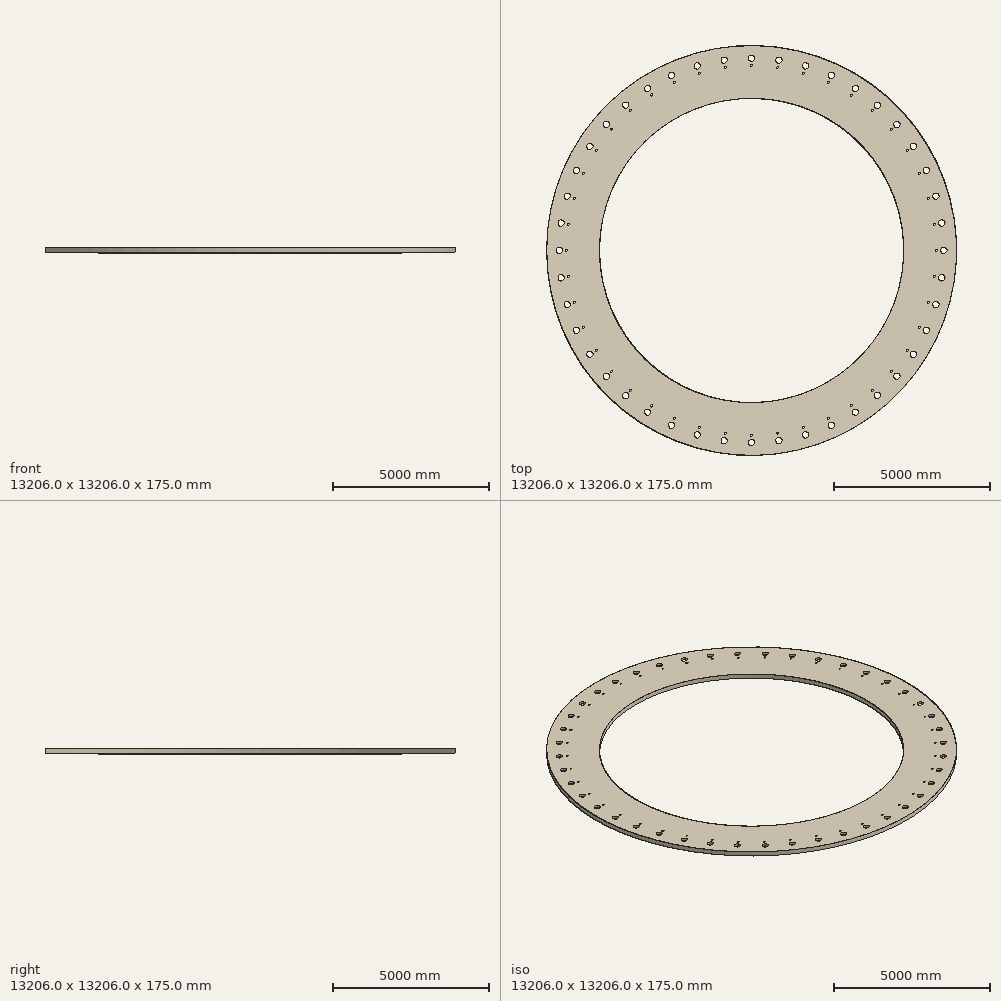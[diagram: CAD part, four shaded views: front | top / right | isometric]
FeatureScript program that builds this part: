
annotation { "Feature Type Name" : "Feature", "Feature Type Description" : "" }
export const myFeature = defineFeature(function(context is Context, id is Id, definition is map)
    precondition{}
    {
        {
            var Q0;
            Q0=qCreatedBy(makeId("Front.planeOp"),FACE);
            var sketch = newSketch(context, id + "F0", { "sketchPlane" : qUnion([Q0])});
            skLineSegment(sketch, "E0", {"start": v(0, 0) * mm, "end": v(0, -150) * mm});
            skLineSegment(sketch, "E1", {"start": v(0, -150) * mm, "end": v(-6, -150) * mm});
            skLineSegment(sketch, "E2", {"start": v(-6, -150) * mm, "end": v(-6, 0) * mm});
            skLineSegment(sketch, "E3", {"start": v(-6, 0) * mm, "end": v(0, 0) * mm});
            skLineSegment(sketch, "E4", {"start": v(-1708, 25) * mm, "end": v(-1708, -125) * mm});
            skLineSegment(sketch, "E5", {"start": v(-1708, -125) * mm, "end": v(-1702, -125) * mm});
            skLineSegment(sketch, "E6", {"start": v(-1702, -125) * mm, "end": v(-1702, 25) * mm});
            skLineSegment(sketch, "E7", {"start": v(-1702, 25) * mm, "end": v(-1708, 25) * mm});
            skLineSegment(sketch, "E8", {"start": v(-1702, 25) * mm, "end": v(-6, 0) * mm});
            skLineSegment(sketch, "E9.0", {"start": v(-1702, -50) * mm, "end": v(-6, -75) * mm});
            skLineSegment(sketch, "E10", {"start": v(0, 0) * mm, "end": v(4895, 0) * mm, "construction": true});
            skPoint(sketch, "E11", {"position": v(4895, 0) * mm});
            skLineSegment(sketch, "E12", {"start": v(4895, 0) * mm, "end": v(4895, 100) * mm, "construction": true});
            skSolve(sketch);
        }
        {
            var Q0;
            Q0 = qSketchRegion(id + "F0", true);
            var Q1;
            Q1=sQuery(id+"F0.wireOp",EDGE,"E12");
            revolve(context, id + "F1", {"surfaceOperationType" : NewSurfaceOperationType.NEW, "entities" : qUnion([Q0]), "axis" : qUnion([Q1]), "revolveType" : RevolveType.FULL});
        }
        {
            var Q0;
            Q0=qCreatedBy(makeId("Top.planeOp"),FACE);
            var sketch = newSketch(context, id + "F2", { "sketchPlane" : qUnion([Q0])});
            skLineSegment(sketch, "E13", {"start": v(0, 0) * mm, "end": v(4895, 0) * mm, "construction": true});
            skLineSegment(sketch, "E14", {"start": v(0, 0) * mm, "end": v(-1055, 0) * mm});
            skLineSegment(sketch, "E15", {"start": v(-1055, 0) * mm, "end": v(-1295, 0) * mm});
            skCircle(sketch, "E16", {"center": v(-1055, 0) * mm, "radius": 35.5 * mm});
            skCircle(sketch, "E17", {"center": v(-1295, 0) * mm, "radius": 102.5 * mm});
            skCircle(sketch, "E18.1.0", {"center": v(-1232, -880.93) * mm, "radius": 102.5 * mm});
            skCircle(sketch, "E18.1.1", {"center": v(-994.44, -846.77) * mm, "radius": 35.5 * mm});
            skCircle(sketch, "E18.2.0", {"center": v(-1044.26, -1743.92) * mm, "radius": 102.5 * mm});
            skCircle(sketch, "E18.2.1", {"center": v(-813.98, -1676.3) * mm, "radius": 35.5 * mm});
            skCircle(sketch, "E18.3.0", {"center": v(-735.62, -2571.42) * mm, "radius": 102.5 * mm});
            skCircle(sketch, "E18.3.1", {"center": v(-517.31, -2471.72) * mm, "radius": 35.5 * mm});
            skCircle(sketch, "E18.4.0", {"center": v(-312.36, -3346.57) * mm, "radius": 102.5 * mm});
            skCircle(sketch, "E18.4.1", {"center": v(-110.46, -3216.81) * mm, "radius": 35.5 * mm});
            skCircle(sketch, "E18.5.0", {"center": v(216.91, -4053.59) * mm, "radius": 102.5 * mm});
            skCircle(sketch, "E18.5.1", {"center": v(398.3, -3896.42) * mm, "radius": 35.5 * mm});
            skCircle(sketch, "E18.6.0", {"center": v(841.41, -4678.09) * mm, "radius": 102.5 * mm});
            skCircle(sketch, "E18.6.1", {"center": v(998.58, -4496.7) * mm, "radius": 35.5 * mm});
            skCircle(sketch, "E18.7.0", {"center": v(1548.43, -5207.36) * mm, "radius": 102.5 * mm});
            skCircle(sketch, "E18.7.1", {"center": v(1678.19, -5005.46) * mm, "radius": 35.5 * mm});
            skCircle(sketch, "E18.8.0", {"center": v(2323.58, -5630.62) * mm, "radius": 102.5 * mm});
            skCircle(sketch, "E18.8.1", {"center": v(2423.28, -5412.31) * mm, "radius": 35.5 * mm});
            skCircle(sketch, "E18.9.0", {"center": v(3151.08, -5939.26) * mm, "radius": 102.5 * mm});
            skCircle(sketch, "E18.9.1", {"center": v(3218.7, -5708.98) * mm, "radius": 35.5 * mm});
            skCircle(sketch, "E18.10.0", {"center": v(4014.07, -6127) * mm, "radius": 102.5 * mm});
            skCircle(sketch, "E18.10.1", {"center": v(4048.23, -5889.44) * mm, "radius": 35.5 * mm});
            skCircle(sketch, "E18.11.0", {"center": v(4895, -6190) * mm, "radius": 102.5 * mm});
            skCircle(sketch, "E18.11.1", {"center": v(4895, -5950) * mm, "radius": 35.5 * mm});
            skCircle(sketch, "E18.12.0", {"center": v(5775.93, -6127) * mm, "radius": 102.5 * mm});
            skCircle(sketch, "E18.12.1", {"center": v(5741.77, -5889.44) * mm, "radius": 35.5 * mm});
            skCircle(sketch, "E18.13.0", {"center": v(6638.92, -5939.26) * mm, "radius": 102.5 * mm});
            skCircle(sketch, "E18.13.1", {"center": v(6571.3, -5708.98) * mm, "radius": 35.5 * mm});
            skCircle(sketch, "E18.14.0", {"center": v(7466.42, -5630.62) * mm, "radius": 102.5 * mm});
            skCircle(sketch, "E18.14.1", {"center": v(7366.72, -5412.31) * mm, "radius": 35.5 * mm});
            skCircle(sketch, "E18.15.0", {"center": v(8241.57, -5207.36) * mm, "radius": 102.5 * mm});
            skCircle(sketch, "E18.15.1", {"center": v(8111.81, -5005.46) * mm, "radius": 35.5 * mm});
            skCircle(sketch, "E18.16.0", {"center": v(8948.59, -4678.09) * mm, "radius": 102.5 * mm});
            skCircle(sketch, "E18.16.1", {"center": v(8791.42, -4496.7) * mm, "radius": 35.5 * mm});
            skCircle(sketch, "E18.17.0", {"center": v(9573.09, -4053.59) * mm, "radius": 102.5 * mm});
            skCircle(sketch, "E18.17.1", {"center": v(9391.7, -3896.42) * mm, "radius": 35.5 * mm});
            skCircle(sketch, "E18.18.0", {"center": v(10102.36, -3346.57) * mm, "radius": 102.5 * mm});
            skCircle(sketch, "E18.18.1", {"center": v(9900.46, -3216.81) * mm, "radius": 35.5 * mm});
            skCircle(sketch, "E18.19.0", {"center": v(10525.62, -2571.42) * mm, "radius": 102.5 * mm});
            skCircle(sketch, "E18.19.1", {"center": v(10307.31, -2471.72) * mm, "radius": 35.5 * mm});
            skCircle(sketch, "E18.20.0", {"center": v(10834.26, -1743.92) * mm, "radius": 102.5 * mm});
            skCircle(sketch, "E18.20.1", {"center": v(10603.98, -1676.3) * mm, "radius": 35.5 * mm});
            skCircle(sketch, "E18.21.0", {"center": v(11022, -880.93) * mm, "radius": 102.5 * mm});
            skCircle(sketch, "E18.21.1", {"center": v(10784.44, -846.77) * mm, "radius": 35.5 * mm});
            skCircle(sketch, "E18.22.0", {"center": v(11085, 0) * mm, "radius": 102.5 * mm});
            skCircle(sketch, "E18.22.1", {"center": v(10845, 0) * mm, "radius": 35.5 * mm});
            skCircle(sketch, "E18.23.0", {"center": v(11022, 880.93) * mm, "radius": 102.5 * mm});
            skCircle(sketch, "E18.23.1", {"center": v(10784.44, 846.77) * mm, "radius": 35.5 * mm});
            skCircle(sketch, "E18.24.0", {"center": v(10834.26, 1743.92) * mm, "radius": 102.5 * mm});
            skCircle(sketch, "E18.24.1", {"center": v(10603.98, 1676.3) * mm, "radius": 35.5 * mm});
            skCircle(sketch, "E18.25.0", {"center": v(10525.62, 2571.42) * mm, "radius": 102.5 * mm});
            skCircle(sketch, "E18.25.1", {"center": v(10307.31, 2471.72) * mm, "radius": 35.5 * mm});
            skCircle(sketch, "E18.26.0", {"center": v(10102.36, 3346.57) * mm, "radius": 102.5 * mm});
            skCircle(sketch, "E18.26.1", {"center": v(9900.46, 3216.81) * mm, "radius": 35.5 * mm});
            skCircle(sketch, "E18.27.0", {"center": v(9573.09, 4053.59) * mm, "radius": 102.5 * mm});
            skCircle(sketch, "E18.27.1", {"center": v(9391.7, 3896.42) * mm, "radius": 35.5 * mm});
            skCircle(sketch, "E18.28.0", {"center": v(8948.59, 4678.09) * mm, "radius": 102.5 * mm});
            skCircle(sketch, "E18.28.1", {"center": v(8791.42, 4496.7) * mm, "radius": 35.5 * mm});
            skCircle(sketch, "E18.29.0", {"center": v(8241.57, 5207.36) * mm, "radius": 102.5 * mm});
            skCircle(sketch, "E18.29.1", {"center": v(8111.81, 5005.46) * mm, "radius": 35.5 * mm});
            skCircle(sketch, "E18.30.0", {"center": v(7466.42, 5630.62) * mm, "radius": 102.5 * mm});
            skCircle(sketch, "E18.30.1", {"center": v(7366.72, 5412.31) * mm, "radius": 35.5 * mm});
            skCircle(sketch, "E18.31.0", {"center": v(6638.92, 5939.26) * mm, "radius": 102.5 * mm});
            skCircle(sketch, "E18.31.1", {"center": v(6571.3, 5708.98) * mm, "radius": 35.5 * mm});
            skCircle(sketch, "E18.32.0", {"center": v(5775.93, 6127) * mm, "radius": 102.5 * mm});
            skCircle(sketch, "E18.32.1", {"center": v(5741.77, 5889.44) * mm, "radius": 35.5 * mm});
            skCircle(sketch, "E18.33.0", {"center": v(4895, 6190) * mm, "radius": 102.5 * mm});
            skCircle(sketch, "E18.33.1", {"center": v(4895, 5950) * mm, "radius": 35.5 * mm});
            skCircle(sketch, "E18.34.0", {"center": v(4014.07, 6127) * mm, "radius": 102.5 * mm});
            skCircle(sketch, "E18.34.1", {"center": v(4048.23, 5889.44) * mm, "radius": 35.5 * mm});
            skCircle(sketch, "E18.35.0", {"center": v(3151.08, 5939.26) * mm, "radius": 102.5 * mm});
            skCircle(sketch, "E18.35.1", {"center": v(3218.7, 5708.98) * mm, "radius": 35.5 * mm});
            skCircle(sketch, "E18.36.0", {"center": v(2323.58, 5630.62) * mm, "radius": 102.5 * mm});
            skCircle(sketch, "E18.36.1", {"center": v(2423.28, 5412.31) * mm, "radius": 35.5 * mm});
            skCircle(sketch, "E18.37.0", {"center": v(1548.43, 5207.36) * mm, "radius": 102.5 * mm});
            skCircle(sketch, "E18.37.1", {"center": v(1678.19, 5005.46) * mm, "radius": 35.5 * mm});
            skCircle(sketch, "E18.38.0", {"center": v(841.41, 4678.09) * mm, "radius": 102.5 * mm});
            skCircle(sketch, "E18.38.1", {"center": v(998.58, 4496.7) * mm, "radius": 35.5 * mm});
            skCircle(sketch, "E18.39.0", {"center": v(216.91, 4053.59) * mm, "radius": 102.5 * mm});
            skCircle(sketch, "E18.39.1", {"center": v(398.3, 3896.42) * mm, "radius": 35.5 * mm});
            skCircle(sketch, "E18.40.0", {"center": v(-312.36, 3346.57) * mm, "radius": 102.5 * mm});
            skCircle(sketch, "E18.40.1", {"center": v(-110.46, 3216.81) * mm, "radius": 35.5 * mm});
            skCircle(sketch, "E18.41.0", {"center": v(-735.62, 2571.42) * mm, "radius": 102.5 * mm});
            skCircle(sketch, "E18.41.1", {"center": v(-517.31, 2471.72) * mm, "radius": 35.5 * mm});
            skCircle(sketch, "E18.42.0", {"center": v(-1044.26, 1743.92) * mm, "radius": 102.5 * mm});
            skCircle(sketch, "E18.42.1", {"center": v(-813.98, 1676.3) * mm, "radius": 35.5 * mm});
            skCircle(sketch, "E18.43.0", {"center": v(-1232, 880.93) * mm, "radius": 102.5 * mm});
            skCircle(sketch, "E18.43.1", {"center": v(-994.44, 846.77) * mm, "radius": 35.5 * mm});
            skPoint(sketch, "E18.center", {"position": v(4895, 0) * mm});
            skSolve(sketch);
        }
        {
            var Q0;
            Q0 = qSketchRegion(id + "F2", true);
            extrude(context, id + "F3", {"entities" : qUnion([Q0]), "operationType" : NewBodyOperationType.REMOVE, "endBound" : BoundingType.THROUGH_ALL, "depth" : 25 * mm, "offsetDistance" : 25 * mm, "hasSecondDirection" : true, "secondDirectionBound" : BoundingType.THROUGH_ALL, "secondDirectionOppositeDirection" : true, "secondDirectionDepth" : 25 * mm});
        }
    });
